# Revit family: ASSA_ABLOY_VersaMax_Fold02
name_source: partatom
category: Doors
units: mm (PartAtom-declared; Revit-internal decimal feet)

## family parameters
Always vertical = Yes
Cut with Voids When Loaded = No
Host = Wall
OmniClass Number = 23.30.10.00
OmniClass Title = Doors
Room Calculation Point = No
Shared = No

## types (1)
- ASSA_ABLOY_VersaMax_Fold02
    Analytic Construction = <None>
    BIMobject category = Swing Doors
    Bottom Profile Height = Folding Leaf : 0'  4"
    Bottom Profile Option 01 = Folding Leaf : 0'  4"
    Bottom Profile Option 02 = Folding Leaf : 0'  7"
    Bottom Profile Option 03 = Folding Leaf : 0'  10"
    Bottom Profile Option 04 = Folding Leaf : 0'  12"
    Brass Polished Finish = Brass, Polished
    Brass Satin Finish = Brass, Satin
    Clear Anodized = Clear Anodized
    Dark Bronze Anodized = Dark Bronze Anodized
    Date of publishing = 2015-02-23
    Depth = 0.00
    Dimensions Overconstraint = No
    Edition number = 1
    Frame Material = Aluminum
    Function = Interior
    Gap = 0' - 0 1/2"
    Glass = Glass
    Height = 7' - 6"
    IFC Classification = Door
    Jumb Thickness = 0' - 2"
    Leaf Height = 7' - 3 1/2"
    Leaf Width = 2' - 3"
    Manufacturer = ASSA ABLOY Entrance Systems-North America
    Manufacturer name = ASSA ABLOY Entrance Systems-North America
    Material main = Aluminium
    Max. Width = 5' - 11"
    Min. Width = 3' - 4 1/2"
    Nominal height = 0.00
    Nominal width = 0.00
    Optional 1" Jambs = No
    Product SKU = VersaMax_Fold_OHC
    Product data url = http://besam-na.bimobject.com
    Product family = ICU
    Product group = Fold
    QR code = http://besam-na.bimobject.com
    Rough Height = 7' - 6"
    Rough Width = 5' - 0"
    Rubber = Rubber, Black
    Stainless Steel Polished Finish = Stainless Steel, Polished
    Stainless Steel Satin Finish = Stainless Steel, Satin
    Thickness = 0' - 4 1/2"
    Top Profile Height = 0' - 4"
    UNSPSC Code = 30171511
    Uniclass 1.4 Code = L81323
    Uniclass 1.4 Description = Swings
    Wall Closure = By host
    Weight Net (Kg) = 0
    Width = 4' - 11 1/2"

## geometry (parser evidence)
native form markers: Blend x4, Sweep x30
no freeform markers — native parametric forms only
